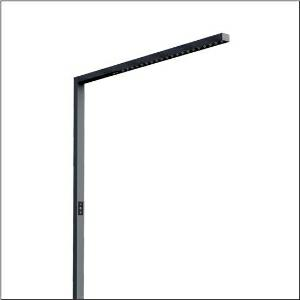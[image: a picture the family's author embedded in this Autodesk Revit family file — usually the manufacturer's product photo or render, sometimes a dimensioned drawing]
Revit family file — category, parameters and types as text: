
# Revit family: silica_r__31_floor_51my52fa4cb_29ea
name_source: partatom
category: Lighting Fixtures
units: mm (PartAtom-declared; Revit-internal decimal feet)

## family parameters
Cut with Voids When Loaded = No
Host = Face
Light Source = No
Part Type = Normal
Room Calculation Point = No
Round Connector Dimension = Use Diameter
Shared = No

## types (1)
- Silica® 31 Floor (1 x LED, 10600 lm, 75 W, 4000K)
    Apparent Load = 75 VA
    CIE Flux Codes = 86 100 100 24 100
    Color Rendering = 80
    Color Temperature = 4000K
    Default Elevation = 1800 mm
    Description = Silica® 31 Floor, floorstanding luminaire, secondary optical cover: cover panel, of PMMA, light emission: direct/indirect distribution, primary light characteristic: symmetric, installation type: not mounted, LED, rated luminous flux: 10.600lm, luminous efficacy: 141lm/W, light colour: 840, colour temperature: 4000K, control gear: Touchdim, daylight-dependent control, with cable with plug, mains connection: 230V, AC, 50Hz, connection cable pre-assembled, rated input power: 75W, luminaire head, of aluminium, jet black (RAL 9005), length: 1.203mm, width: 52mm, supporting column, angular, of aluminium, jet black (RAL 9005), baseplate, of steel, jet black (RAL 9005), protection rating (complete): IP20, insulation class (complete): insulation class I (protective earthing), certification: CE, permissible operating ambient temperature: -20..+40°C, standard: EN 50419, packaging unit: 1 piece
    Height = 36 mm
    Lamp = 1 x LED
    Lamp Light Flux = 10600 lm
    Lamp Power = 75 W
    Lamp count = 1
    Length = 1203 mm
    Luminous efficacy = 141 lm/W
    Manufacturer = Siteco
    ModVariant = No
    Model = 51MY52FA4CB
    Mounting Place = Floor
    Mounting Type = Freestanding
    Number of Poles = 1
    OnlyDefault = Yes
    Power Factor = 1
    Product Name = Silica® 31 Floor
    Product group = floorstanding luminaire
    ProductGroupID = 1302
    Protection Class = Protection class I
    Protection Degree = IP 20
    RLX_Detail_Level = 1
    RLX_Emergency_Light_Flux = 0 lm
    RLX_Emergency_Type = 0
    RLX_Emergency_Type_DB = No
    RlxData = <blob elided: 20125 chars, md5=77d2bb8f>
    Socket = socket
    Standby Power = 0 W
    System Light Flux = 10600 lm
    System Power = 75 W
    Type Comments = Product without accessories
    Type Image = l_1275297.jpg
    URL = http://relux.com
    VarID = ---
    Voltage = 0 V
    Weight = 0.00 kg
    Width = 52 mm

## geometry (parser evidence)
native form markers: Blend x4, Sweep x14
no freeform markers — native parametric forms only
